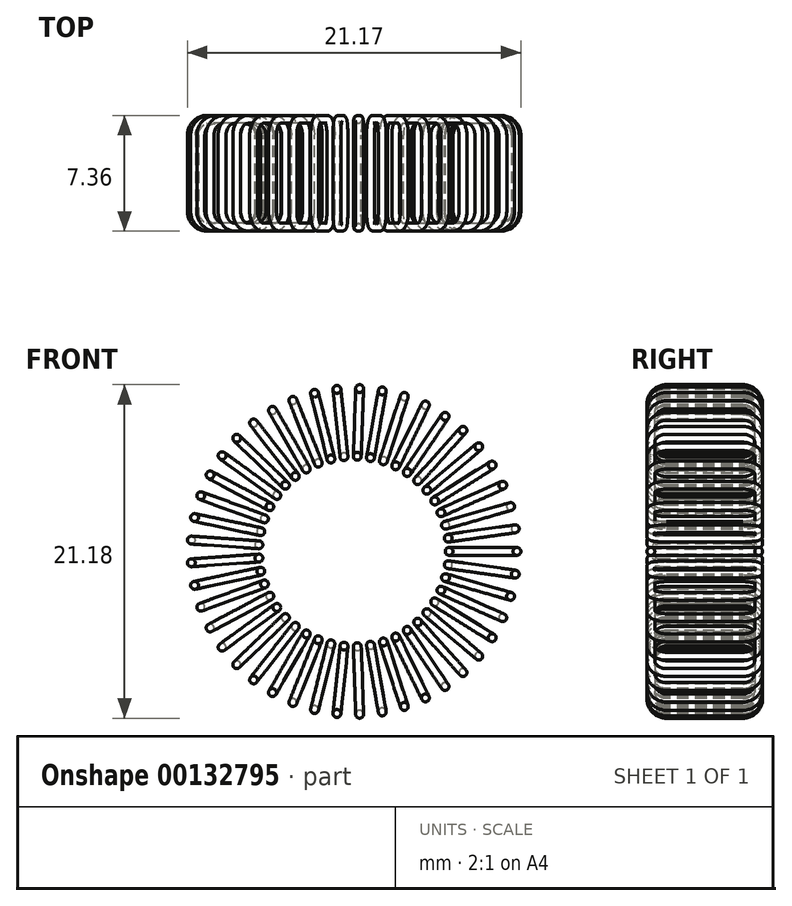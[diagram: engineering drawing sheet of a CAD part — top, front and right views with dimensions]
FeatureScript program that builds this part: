
annotation { "Feature Type Name" : "Feature", "Feature Type Description" : "" }
export const myFeature = defineFeature(function(context is Context, id is Id, definition is map)
    precondition{}
    {
        {
            var Q0;
            Q0=qCreatedBy(makeId("Top.planeOp"),FACE);
            var sketch = newSketch(context, id + "F0", { "sketchPlane" : qUnion([Q0])});
            skLineSegment(sketch, "E0.bottom", {"start": v(7.05, 3.43) * mm, "end": v(9.35, 3.43) * mm});
            skLineSegment(sketch, "E0.left", {"start": v(6.05, 2.43) * mm, "end": v(6.05, 0) * mm});
            skLineSegment(sketch, "E0.right", {"start": v(10.35, 2.43) * mm, "end": v(10.35, 0) * mm});
            skPoint(sketch, "E1.visualSharp", {"position": v(6.05, 3.43) * mm});
            skArc(sketch, "E1.filletArc", {"start": v(7.05, 3.43) * mm, "mid": v(6.34, 3.13) * mm, "end": v(6.05, 2.43) * mm});
            skPoint(sketch, "E2.visualSharp", {"position": v(10.35, 3.43) * mm});
            skArc(sketch, "E2.filletArc", {"start": v(10.35, 2.43) * mm, "mid": v(10.06, 3.13) * mm, "end": v(9.35, 3.43) * mm});
            skSolve(sketch);
        }
        {
            var Q0;
            Q0=qCreatedBy(makeId("Front.planeOp"),FACE);
            var sketch = newSketch(context, id + "F1", { "sketchPlane" : qUnion([Q0])});
            skCircle(sketch, "E3", {"center": v(6.05, 0) * mm, "radius": 0.25 * mm});
            skSolve(sketch);
        }
        {
            var Q0;
            Q0=qSketchRegion(id+"F1",true);
            var Q1;
            Q1=qConstructionFilter(qBodyType(qCreatedBy(id+"F0",EDGE),BodyType.WIRE),ConstructionObject.NO);
            sweep(context, id + "F2", {"profiles" : qUnion([Q0]), "path" : qUnion([Q1])});
        }
        {
            var Q0;
            Q0=makeQuery(id+"F2.opSweep","SWEPT_BODY",BODY,{"disambiguationData":[OSD([sQuery(id+"F0.wireOp",EDGE,"E0.left"),sQuery(id+"F1.wireOp",EDGE,"E3")])]});
            var Q1;
            Q1=qCreatedBy(makeId("Front.planeOp"),FACE);
            mirror(context, id + "F3", {"operationType" : NewBodyOperationType.ADD, "entities" : qUnion([Q0]), "mirrorPlane" : qUnion([Q1])});
        }
        {
            var Q0;
            Q0=qCreatedBy(makeId("Front.planeOp"),FACE);
            var sketch = newSketch(context, id + "F4", { "sketchPlane" : qUnion([Q0])});
            skCircle(sketch, "E4", {"center": v(0, 0) * mm, "radius": 3.71 * mm});
            skSolve(sketch);
        }
        {
            var Q0;
            Q0=makeQuery(id+"F2.opSweep","SWEPT_BODY",BODY,{"disambiguationData":[OSD([sQuery(id+"F0.wireOp",EDGE,"E0.left"),sQuery(id+"F1.wireOp",EDGE,"E3")])]});
            var Q1;
            Q1=sQuery(id+"F4.wireOp",EDGE,"E4");
            circularPattern(context, id + "F5", {"entities" : qUnion([Q0]), "axis" : qUnion([Q1]), "angle" : 8 * degree, "instanceCount" : 49});
        }
    });
